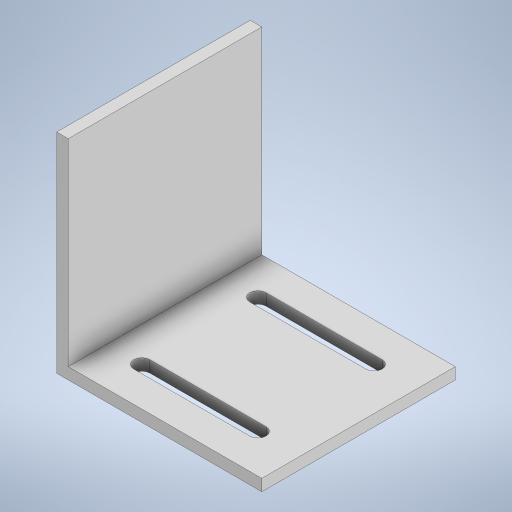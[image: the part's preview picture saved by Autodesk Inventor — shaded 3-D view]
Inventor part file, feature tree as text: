
AUTODESK INVENTOR PART (.ipt)
format: ipt  version: 2024 (Build 280153000, 153)  size: 244,224 bytes
history: native  units: in
note: dims shown in document units (in); Inventor stores cm internally (conversion verified against a paired STEP export)
features: extrude x3, sketch x3
ambient origin geometry x8: Origin, YZ Plane, XZ Plane, XY Plane, X Axis, Y Axis, Z Axis, Center Point
bodies: Solid1 (feature_tree)
feature tree (6):
  extrude  "Extrusion1"  Depth=1.9685in
  extrude  "Extrusion2"  Depth=0.1181in
  extrude  "Extrusion3"  Depth=0.165in
  sketch  "Sketch1"  dims[d0=2.0866in d1=1.9685in]
  sketch  "Sketch2"  dims[d2=0.1181in d3=0.0in d4=0.1181in]
  sketch  "Sketch3"  dims[d5=2.0079in d6=0.0in d7=0.4331in d8=0.1654in d9=1.1811in d10=0.165in d11=0.433in d12=0.165in d13=0.165in d14=1.1811in d15=0.3935in d16=0.3939in d17=0.4921in d18=0.0in]
